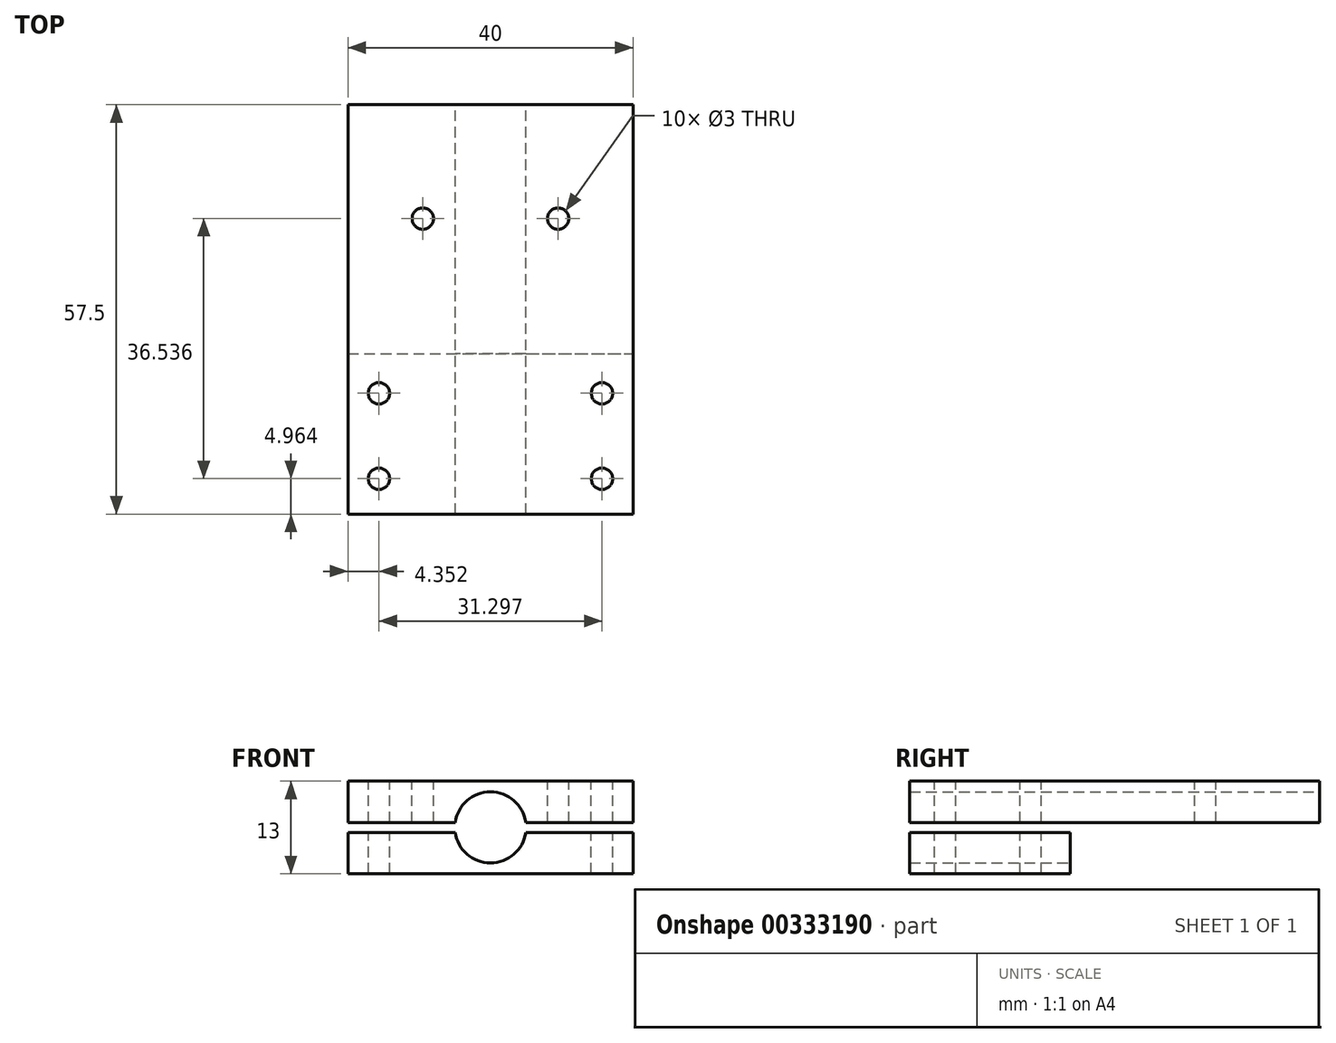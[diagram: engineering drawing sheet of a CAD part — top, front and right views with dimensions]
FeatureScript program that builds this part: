
annotation { "Feature Type Name" : "Feature", "Feature Type Description" : "" }
export const myFeature = defineFeature(function(context is Context, id is Id, definition is map)
    precondition{}
    {
        {
            var Q0;
            Q0=qCreatedBy(makeId("Front.planeOp"),FACE);
            var sketch = newSketch(context, id + "F0", { "sketchPlane" : qUnion([Q0])});
            skArc(sketch, "E0", {"start": v(-4.95, -0.7) * mm, "mid": v(0, -5) * mm, "end": v(4.95, -0.7) * mm});
            skLineSegment(sketch, "E1.bottom", {"start": v(20, -6.5) * mm, "end": v(-20, -6.5) * mm});
            skLineSegment(sketch, "E1.top", {"start": v(20, 6.5) * mm, "end": v(-20, 6.5) * mm});
            skLineSegment(sketch, "E1.left", {"start": v(20, -6.5) * mm, "end": v(20, -0.7) * mm});
            skLineSegment(sketch, "E1.right", {"start": v(-20, -6.5) * mm, "end": v(-20, 6.5) * mm});
            skLineSegment(sketch, "E2.bottom", {"start": v(20, -0.7) * mm, "end": v(4.95, -0.7) * mm});
            skLineSegment(sketch, "E2.top", {"start": v(20, 0.7) * mm, "end": v(4.95, 0.7) * mm});
            skArc(sketch, "E3.trimOffspring", {"start": v(4.95, 0.7) * mm, "mid": v(0, 5) * mm, "end": v(-4.95, 0.7) * mm});
            skLineSegment(sketch, "E4.trimOffspring", {"start": v(-4.95, 0.7) * mm, "end": v(-20, 0.7) * mm});
            skLineSegment(sketch, "E5.trimOffspring", {"start": v(-4.95, -0.7) * mm, "end": v(-20, -0.7) * mm});
            skLineSegment(sketch, "E6.trimOffspring", {"start": v(20, 0.7) * mm, "end": v(20, 6.5) * mm});
            skSolve(sketch);
        }
        {
            var Q0;
            Q0=qSketchRegion(id+"F0",true);
            extrude(context, id + "F1", {"entities" : qUnion([Q0]), "depth" : 45 * mm});
        }
        {
            var Q0;
            Q0=makeQuery(id+"F1.opExtrude","SWEPT_FACE",FACE,{"disambiguationData":[OSD([sQuery(id+"F0.wireOp",EDGE,"E1.top")])]});
            var sketch = newSketch(context, id + "F2", { "sketchPlane" : qUnion([Q0])});
            skLineSegment(sketch, "E7", {"start": v(20, -22.5) * mm, "end": v(-20, -22.5) * mm});
            skSolve(sketch);
        }
        {
            var Q0;
            {var subQ0=sQuery(id+"F2.wireOp",EDGE,"E7");Q0=makeQuery(id+"F2.imprint","IMPRINT",FACE,{"disambiguationData":[TD([[makeQuery(id+"F2.imprint","IMPRINT",EDGE,{"derivedFrom":subQ0}),-1.0]])]});}
            extrude(context, id + "F3", {"entities" : qUnion([Q0]), "operationType" : NewBodyOperationType.REMOVE, "oppositeDirection" : true, "depth" : 25 * mm});
        }
        {
            var Q0;
            {var subQ1=sQuery(id+"F0.wireOp",EDGE,"E1.top");Q0=makeQuery(id+"F3.boolean.opBoolean","COPY",FACE,{"disambiguationData":[TD([makeQuery(id+"F1.opExtrude","SWEPT_FACE",FACE,{"disambiguationData":[OSD([subQ1])]})])],"derivedFrom":makeQuery(id+"F3.opExtrude","SWEPT_FACE",FACE,{"disambiguationData":[OSD([sQuery(id+"F2.wireOp",EDGE,"E7")])]})});}
            var sketch = newSketch(context, id + "F4", { "sketchPlane" : qUnion([Q0])});
            skLineSegment(sketch, "E8.bottom", {"start": v(-20, 6.5) * mm, "end": v(20, 6.5) * mm});
            skLineSegment(sketch, "E8.top", {"start": v(-20, 0.7) * mm, "end": v(20, 0.7) * mm});
            skLineSegment(sketch, "E8.left", {"start": v(-20, 6.5) * mm, "end": v(-20, 0.7) * mm});
            skLineSegment(sketch, "E8.right", {"start": v(20, 6.5) * mm, "end": v(20, 0.7) * mm});
            skSolve(sketch);
        }
        {
            var Q0;
            Q0=makeQuery(id+"F3.boolean.opBoolean","COPY",FACE,{"disambiguationData":[TD([makeQuery(id+"F1.opExtrude","SWEPT_FACE",FACE,{"disambiguationData":[OSD([sQuery(id+"F0.wireOp",EDGE,"E0")])]})])],"derivedFrom":makeQuery(id+"F3.opExtrude","SWEPT_FACE",FACE,{"disambiguationData":[OSD([sQuery(id+"F2.wireOp",EDGE,"E7")])]})});
            var sketch = newSketch(context, id + "F5", { "sketchPlane" : qUnion([Q0])});
            skLineSegment(sketch, "E9.bottom", {"start": v(-20, -0.7) * mm, "end": v(20, -0.7) * mm});
            skLineSegment(sketch, "E9.top", {"start": v(-20, -6.5) * mm, "end": v(20, -6.5) * mm});
            skLineSegment(sketch, "E9.left", {"start": v(-20, -0.7) * mm, "end": v(-20, -6.5) * mm});
            skLineSegment(sketch, "E9.right", {"start": v(20, -0.7) * mm, "end": v(20, -6.5) * mm});
            skSolve(sketch);
        }
        {
            var Q0;
            Q0=qSketchRegion(id+"F4",true);
            var Q1;
            Q1=qSketchRegion(id+"F5",true);
            extrude(context, id + "F6", {"entities" : qUnion([Q0, Q1]), "depth" : 25 * mm});
        }
        {
            var Q0;
            Q0=makeQuery(id+"F1.opExtrude","SWEPT_BODY",BODY,{"disambiguationData":[OSD([sQuery(id+"F0.wireOp",EDGE,"E1.top"),sQuery(id+"F0.wireOp",EDGE,"E1.right"),sQuery(id+"F0.wireOp",EDGE,"E2.top"),sQuery(id+"F0.wireOp",EDGE,"E3.trimOffspring"),sQuery(id+"F0.wireOp",EDGE,"E4.trimOffspring"),sQuery(id+"F0.wireOp",EDGE,"E6.trimOffspring")])]});
            var Q1;
            Q1=makeQuery(id+"F6.opExtrude","SWEPT_BODY",BODY,{"disambiguationData":[OSD([sQuery(id+"F4.wireOp",EDGE,"E8.bottom"),sQuery(id+"F4.wireOp",EDGE,"E8.top"),sQuery(id+"F4.wireOp",EDGE,"E8.left"),sQuery(id+"F4.wireOp",EDGE,"E8.right")])]});
            booleanBodies(context, id + "F7", {"operationType" : BooleanOperationType.UNION, "tools" : qUnion([Q0, Q1])});
        }
        {
            var Q0;
            Q0=makeQuery(id+"F6.opExtrude","CAP_FACE",FACE,{"disambiguationData":[OSD([sQuery(id+"F4.wireOp",EDGE,"E8.bottom"),sQuery(id+"F4.wireOp",EDGE,"E8.top"),sQuery(id+"F4.wireOp",EDGE,"E8.left"),sQuery(id+"F4.wireOp",EDGE,"E8.right")])],"isStart":false});
            var Q1;
            Q1=makeQuery(id+"F6.opExtrude","CAP_FACE",FACE,{"disambiguationData":[OSD([sQuery(id+"F5.wireOp",EDGE,"E9.bottom"),sQuery(id+"F5.wireOp",EDGE,"E9.top"),sQuery(id+"F5.wireOp",EDGE,"E9.left"),sQuery(id+"F5.wireOp",EDGE,"E9.right")])],"isStart":false});
            extrude(context, id + "F8", {"entities" : qUnion([Q0, Q1]), "operationType" : NewBodyOperationType.ADD, "depth" : 10 * mm});
        }
        {
            var Q0;
            Q0=makeQuery(id+"F7.opBoolean","MERGE",FACE,{"derivedFrom":[makeQuery(id+"F1.opExtrude","SWEPT_FACE",FACE,{"disambiguationData":[OSD([sQuery(id+"F0.wireOp",EDGE,"E1.top")])]}),makeQuery(id+"F6.opExtrude","SWEPT_FACE",FACE,{"disambiguationData":[OSD([sQuery(id+"F4.wireOp",EDGE,"E8.bottom")])]})]});
            var sketch = newSketch(context, id + "F9", { "sketchPlane" : qUnion([Q0])});
            skLineSegment(sketch, "E10.direction1", {"start": v(0, 6) * mm, "end": v(25, 6) * mm, "construction": true});
            skLineSegment(sketch, "E10.direction2", {"start": v(0, 6) * mm, "end": v(0, -13) * mm, "construction": true});
            skCircle(sketch, "E11", {"center": v(-15.65, -40.04) * mm, "radius": 1.5 * mm});
            skCircle(sketch, "E12.0.1.0", {"center": v(-15.65, -28.04) * mm, "radius": 1.5 * mm});
            skLineSegment(sketch, "E12.direction1", {"start": v(-15.65, -40.04) * mm, "end": v(9.35, -40.04) * mm, "construction": true});
            skLineSegment(sketch, "E12.direction2", {"start": v(-15.65, -40.04) * mm, "end": v(-15.65, -28.04) * mm, "construction": true});
            skCircle(sketch, "E13.MirrorC", {"center": v(15.65, -40.04) * mm, "radius": 1.5 * mm});
            skCircle(sketch, "E14.MirrorC", {"center": v(15.65, -28.04) * mm, "radius": 1.5 * mm});
            skCircle(sketch, "E15.1.0", {"center": v(9.5, -3.5) * mm, "radius": 1.5 * mm});
            skCircle(sketch, "E15.1.1", {"center": v(-9.5, -3.5) * mm, "radius": 1.5 * mm});
            skPoint(sketch, "E15.center", {"position": v(0, -3.5) * mm});
            skSolve(sketch);
        }
        {
            var Q0;
            Q0=qSketchRegion(id+"F9",true);
            extrude(context, id + "F10", {"entities" : qUnion([Q0]), "operationType" : NewBodyOperationType.REMOVE, "oppositeDirection" : true, "depth" : 25 * mm});
        }
        {
            var Q0;
            Q0=makeQuery(id+"F6.opExtrude","CAP_FACE",FACE,{"disambiguationData":[OSD([sQuery(id+"F4.wireOp",EDGE,"E8.bottom"),sQuery(id+"F4.wireOp",EDGE,"E8.top"),sQuery(id+"F4.wireOp",EDGE,"E8.left"),sQuery(id+"F4.wireOp",EDGE,"E8.right")])],"isStart":true});
            var Q1;
            Q1=makeQuery(id+"F6.opExtrude","CAP_FACE",FACE,{"disambiguationData":[OSD([sQuery(id+"F5.wireOp",EDGE,"E9.bottom"),sQuery(id+"F5.wireOp",EDGE,"E9.top"),sQuery(id+"F5.wireOp",EDGE,"E9.left"),sQuery(id+"F5.wireOp",EDGE,"E9.right")])],"isStart":true});
            extrude(context, id + "F11", {"entities" : qUnion([Q0, Q1]), "operationType" : NewBodyOperationType.REMOVE, "oppositeDirection" : true, "depth" : 56.4 * mm});
        }
    });
